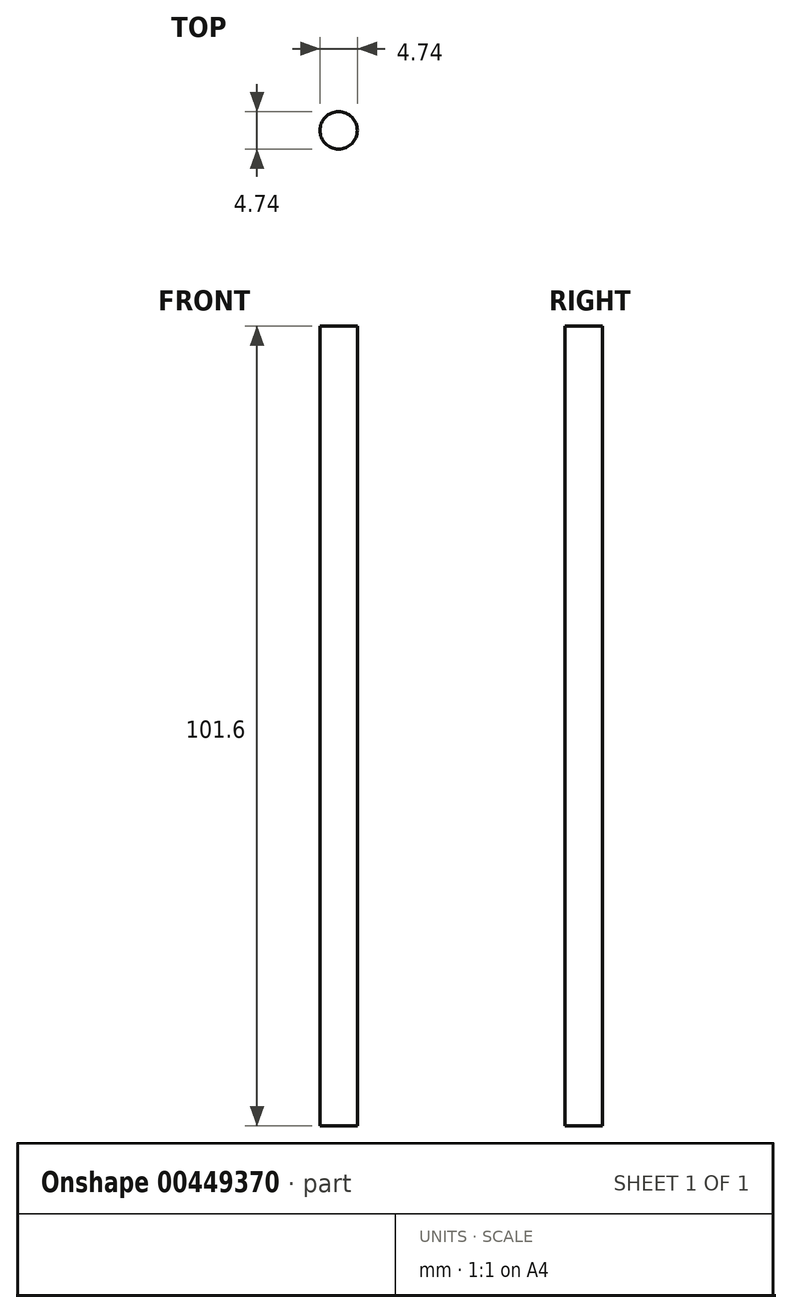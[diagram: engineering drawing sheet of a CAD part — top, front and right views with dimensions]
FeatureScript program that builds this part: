
annotation { "Feature Type Name" : "Feature", "Feature Type Description" : "" }
export const myFeature = defineFeature(function(context is Context, id is Id, definition is map)
    precondition{}
    {
        {
            var Q0;
            Q0=qCreatedBy(makeId("Top.planeOp"),FACE);
            var sketch = newSketch(context, id + "F0", { "sketchPlane" : qUnion([Q0])});
            skCircle(sketch, "E0", {"center": v(0, 0) * mm, "radius": 2.37 * mm});
            skSolve(sketch);
        }
        {
            var Q0;
            Q0 = qSketchRegion(id + "F0", true);
            extrude(context, id + "F1", {"entities" : qUnion([Q0]), "oppositeDirection" : true, "depth" : 101.6 * mm});
        }
    });
